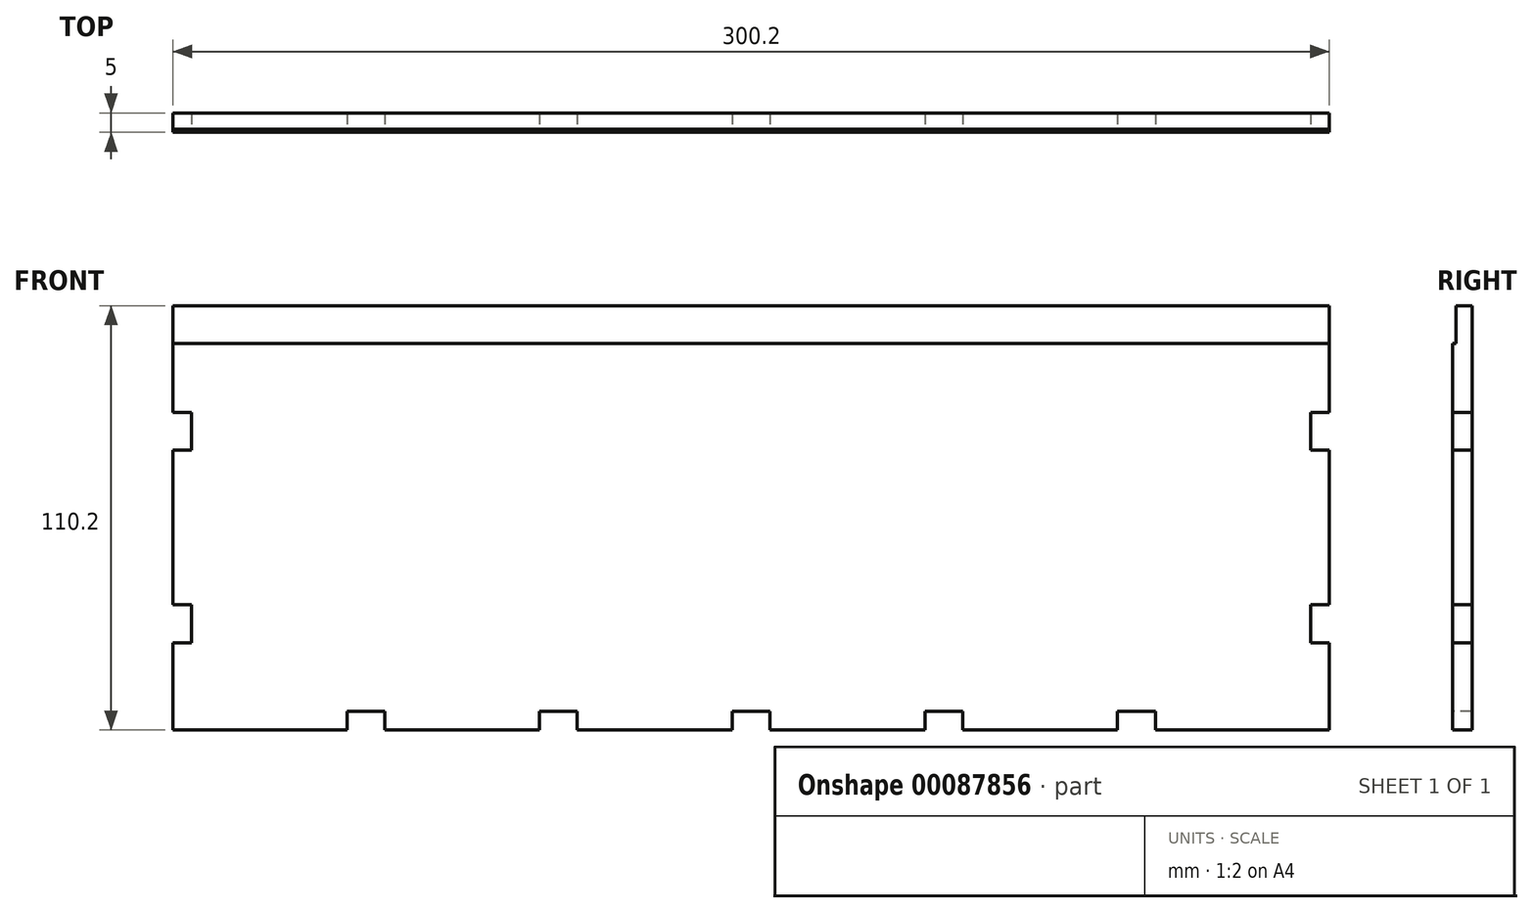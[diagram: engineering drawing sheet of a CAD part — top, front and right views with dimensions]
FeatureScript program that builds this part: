
annotation { "Feature Type Name" : "Feature", "Feature Type Description" : "" }
export const myFeature = defineFeature(function(context is Context, id is Id, definition is map)
    precondition{}
    {
        {
            var Q0;
            Q0=qCreatedBy(makeId("Front.planeOp"),FACE);
            var sketch = newSketch(context, id + "F0", { "sketchPlane" : qUnion([Q0])});
            skLineSegment(sketch, "E0.bottom", {"start": v(150.1, 55.1) * mm, "end": v(-150.1, 55.1) * mm});
            skLineSegment(sketch, "E0.top", {"start": v(150.1, -55.1) * mm, "end": v(-150.1, -55.1) * mm});
            skLineSegment(sketch, "E0.left", {"start": v(150.1, 55.1) * mm, "end": v(150.1, -55.1) * mm});
            skLineSegment(sketch, "E0.right", {"start": v(-150.1, 55.1) * mm, "end": v(-150.1, -55.1) * mm});
            skPoint(sketch, "E0.middle", {"position": v(0, 0) * mm});
            skSolve(sketch);
        }
        {
            var Q0;
            Q0=makeQuery(id+"F0.imprint","IMPRINT",FACE,{"disambiguationData":[TD([[makeQuery(id+"F0.imprint","IMPRINT",EDGE,{"derivedFrom":sQuery(id+"F0.wireOp",EDGE,"E0.bottom")}),1.0]])]});
            extrude(context, id + "F1", {"entities" : qUnion([Q0]), "depth" : 5 * mm});
        }
        {
            var Q0;
            Q0=makeQuery(id+"F1.opExtrude","CAP_FACE",FACE,{"disambiguationData":[OSD([sQuery(id+"F0.wireOp",EDGE,"E0.bottom"),sQuery(id+"F0.wireOp",EDGE,"E0.top"),sQuery(id+"F0.wireOp",EDGE,"E0.left"),sQuery(id+"F0.wireOp",EDGE,"E0.right")])],"isStart":false});
            var sketch = newSketch(context, id + "F2", { "sketchPlane" : qUnion([Q0])});
            skLineSegment(sketch, "E1.bottom", {"start": v(-150.1, 55.1) * mm, "end": v(150.1, 55.1) * mm});
            skLineSegment(sketch, "E1.top", {"start": v(-150.1, 45.2) * mm, "end": v(150.1, 45.2) * mm});
            skLineSegment(sketch, "E1.left", {"start": v(-150.1, 55.1) * mm, "end": v(-150.1, 45.2) * mm});
            skLineSegment(sketch, "E1.right", {"start": v(150.1, 55.1) * mm, "end": v(150.1, 45.2) * mm});
            skSolve(sketch);
        }
        {
            var Q0;
            Q0 = qSketchRegion(id + "F2", true);
            extrude(context, id + "F3", {"entities" : qUnion([Q0]), "operationType" : NewBodyOperationType.REMOVE, "oppositeDirection" : true, "depth" : 0.8 * mm});
        }
        {
            var Q0;
            Q0=makeQuery(id+"F1.opExtrude","CAP_FACE",FACE,{"disambiguationData":[OSD([sQuery(id+"F0.wireOp",EDGE,"E0.bottom"),sQuery(id+"F0.wireOp",EDGE,"E0.top"),sQuery(id+"F0.wireOp",EDGE,"E0.left"),sQuery(id+"F0.wireOp",EDGE,"E0.right")])],"isStart":false});
            var sketch = newSketch(context, id + "F4", { "sketchPlane" : qUnion([Q0])});
            skLineSegment(sketch, "E2.bottom", {"start": v(-150.1, 27.4) * mm, "end": v(-145.2, 27.4) * mm});
            skLineSegment(sketch, "E2.top", {"start": v(-150.1, 17.6) * mm, "end": v(-145.2, 17.6) * mm});
            skLineSegment(sketch, "E2.left", {"start": v(-150.1, 27.4) * mm, "end": v(-150.1, 17.6) * mm});
            skLineSegment(sketch, "E2.right", {"start": v(-145.2, 27.4) * mm, "end": v(-145.2, 17.6) * mm});
            skLineSegment(sketch, "E3.bottom", {"start": v(-150.1, -22.6) * mm, "end": v(-145.2, -22.6) * mm});
            skLineSegment(sketch, "E3.top", {"start": v(-150.1, -32.4) * mm, "end": v(-145.2, -32.4) * mm});
            skLineSegment(sketch, "E3.left", {"start": v(-150.1, -22.6) * mm, "end": v(-150.1, -32.4) * mm});
            skLineSegment(sketch, "E3.right", {"start": v(-145.2, -22.6) * mm, "end": v(-145.2, -32.4) * mm});
            skLineSegment(sketch, "E4.bottom", {"start": v(-104.9, -55.1) * mm, "end": v(-95.1, -55.1) * mm});
            skLineSegment(sketch, "E4.top", {"start": v(-104.9, -50.2) * mm, "end": v(-95.1, -50.2) * mm});
            skLineSegment(sketch, "E4.left", {"start": v(-104.9, -55.1) * mm, "end": v(-104.9, -50.2) * mm});
            skLineSegment(sketch, "E4.right", {"start": v(-95.1, -55.1) * mm, "end": v(-95.1, -50.2) * mm});
            skLineSegment(sketch, "E5", {"start": v(-180.07, -2.5) * mm, "end": v(-60.6, -2.5) * mm, "construction": true});
            skLineSegment(sketch, "E6.bottom", {"start": v(-54.9, -55.1) * mm, "end": v(-45.1, -55.1) * mm});
            skLineSegment(sketch, "E6.top", {"start": v(-54.9, -50.2) * mm, "end": v(-45.1, -50.2) * mm});
            skLineSegment(sketch, "E6.left", {"start": v(-54.9, -55.1) * mm, "end": v(-54.9, -50.2) * mm});
            skLineSegment(sketch, "E6.right", {"start": v(-45.1, -55.1) * mm, "end": v(-45.1, -50.2) * mm});
            skLineSegment(sketch, "E7.bottom", {"start": v(-4.9, -50.2) * mm, "end": v(4.9, -50.2) * mm});
            skLineSegment(sketch, "E7.top", {"start": v(-4.9, -55.1) * mm, "end": v(4.9, -55.1) * mm});
            skLineSegment(sketch, "E7.left", {"start": v(-4.9, -50.2) * mm, "end": v(-4.9, -55.1) * mm});
            skLineSegment(sketch, "E7.right", {"start": v(4.9, -50.2) * mm, "end": v(4.9, -55.1) * mm});
            skLineSegment(sketch, "E8.bottom", {"start": v(45.1, -50.2) * mm, "end": v(54.9, -50.2) * mm});
            skLineSegment(sketch, "E8.top", {"start": v(45.1, -55.1) * mm, "end": v(54.9, -55.1) * mm});
            skLineSegment(sketch, "E8.left", {"start": v(45.1, -50.2) * mm, "end": v(45.1, -55.1) * mm});
            skLineSegment(sketch, "E8.right", {"start": v(54.9, -50.2) * mm, "end": v(54.9, -55.1) * mm});
            skLineSegment(sketch, "E9.MirrorCS", {"start": v(150.1, 27.4) * mm, "end": v(150.1, 17.6) * mm});
            skLineSegment(sketch, "E10.MirrorCS", {"start": v(145.2, -22.6) * mm, "end": v(145.2, -32.4) * mm});
            skLineSegment(sketch, "E11.MirrorCS", {"start": v(150.1, -32.4) * mm, "end": v(145.2, -32.4) * mm});
            skLineSegment(sketch, "E12.MirrorCS", {"start": v(150.1, -22.6) * mm, "end": v(145.2, -22.6) * mm});
            skLineSegment(sketch, "E13.MirrorCS", {"start": v(150.1, 27.4) * mm, "end": v(145.2, 27.4) * mm});
            skLineSegment(sketch, "E14.MirrorCS", {"start": v(150.1, 17.6) * mm, "end": v(145.2, 17.6) * mm});
            skLineSegment(sketch, "E15.MirrorCS", {"start": v(150.1, -22.6) * mm, "end": v(150.1, -32.4) * mm});
            skLineSegment(sketch, "E16.MirrorCS", {"start": v(145.2, 27.4) * mm, "end": v(145.2, 17.6) * mm});
            skLineSegment(sketch, "E17.bottom", {"start": v(95.1, -50.2) * mm, "end": v(104.9, -50.2) * mm});
            skLineSegment(sketch, "E17.top", {"start": v(95.1, -55.1) * mm, "end": v(104.9, -55.1) * mm});
            skLineSegment(sketch, "E17.left", {"start": v(95.1, -50.2) * mm, "end": v(95.1, -55.1) * mm});
            skLineSegment(sketch, "E17.right", {"start": v(104.9, -50.2) * mm, "end": v(104.9, -55.1) * mm});
            skSolve(sketch);
        }
        {
            var Q0;
            Q0 = qSketchRegion(id + "F4", true);
            extrude(context, id + "F5", {"entities" : qUnion([Q0]), "operationType" : NewBodyOperationType.REMOVE, "endBound" : BoundingType.UP_TO_NEXT, "oppositeDirection" : true, "depth" : 25 * mm});
        }
    });
